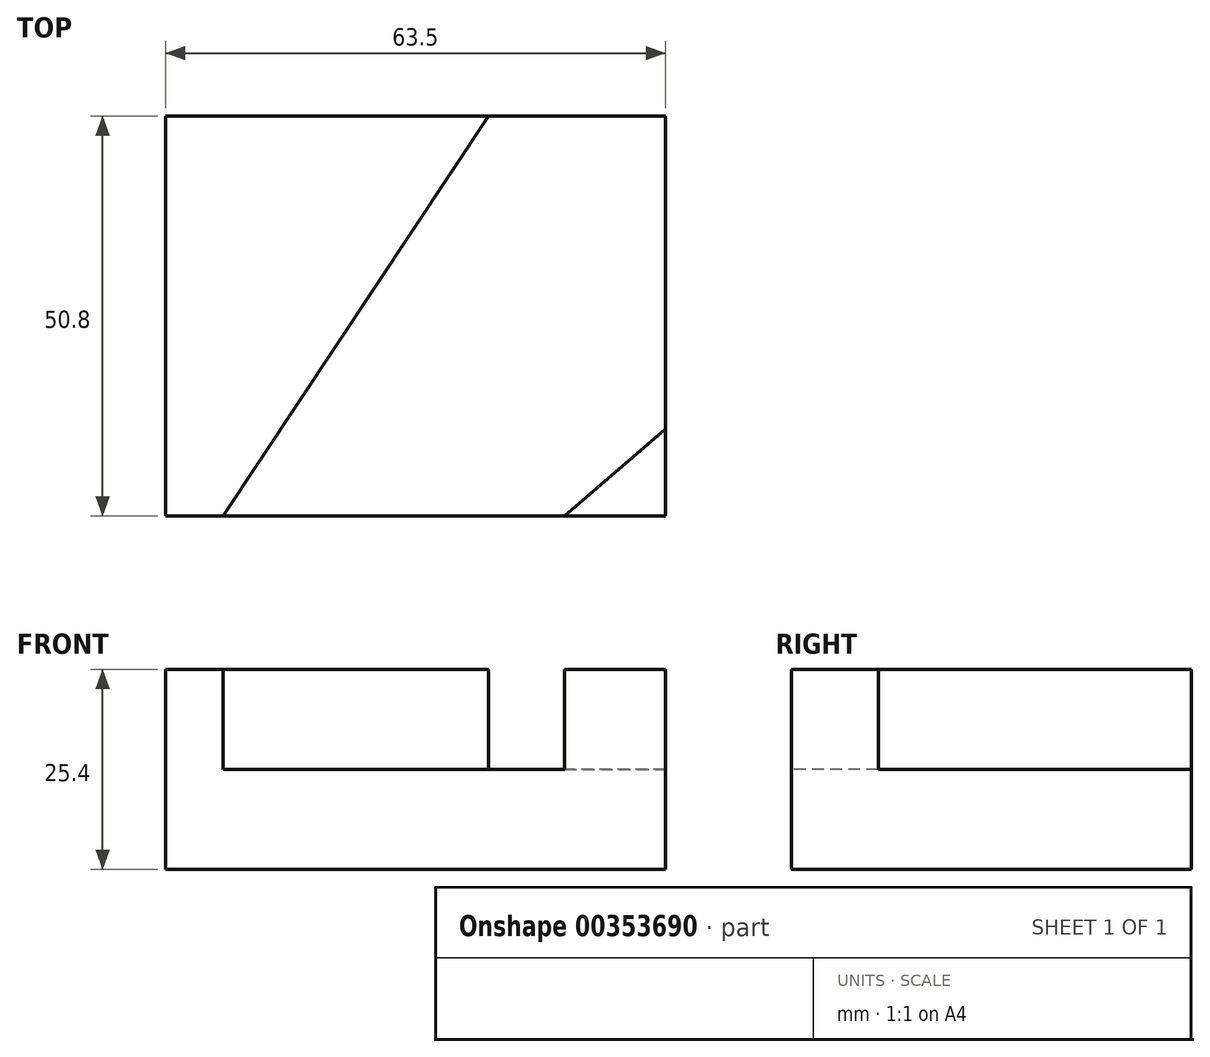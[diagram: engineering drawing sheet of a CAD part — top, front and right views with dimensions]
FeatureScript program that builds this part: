
annotation { "Feature Type Name" : "Feature", "Feature Type Description" : "" }
export const myFeature = defineFeature(function(context is Context, id is Id, definition is map)
    precondition{}
    {
        {
            var Q0;
            Q0=qCreatedBy(makeId("Top.planeOp"),FACE);
            var sketch = newSketch(context, id + "F0", { "sketchPlane" : qUnion([Q0])});
            skLineSegment(sketch, "E0", {"start": v(-35.36, 3.74) * mm, "end": v(-35.36, -47.06) * mm});
            skLineSegment(sketch, "E1", {"start": v(-35.36, -47.06) * mm, "end": v(28.14, -47.06) * mm});
            skLineSegment(sketch, "E2", {"start": v(28.14, -47.06) * mm, "end": v(28.14, 3.74) * mm});
            skLineSegment(sketch, "E3", {"start": v(28.14, 3.74) * mm, "end": v(-35.36, 3.74) * mm});
            skSolve(sketch);
        }
        {
            var Q0;
            Q0 = qSketchRegion(id + "F0", true);
            extrude(context, id + "F1", {"entities" : qUnion([Q0]), "depth" : 25.4 * mm});
        }
        {
            var Q0;
            Q0=makeQuery(id+"F1.opExtrude","CAP_FACE",FACE,{"disambiguationData":[OSD([sQuery(id+"F0.wireOp",EDGE,"E0"),sQuery(id+"F0.wireOp",EDGE,"E1"),sQuery(id+"F0.wireOp",EDGE,"E2"),sQuery(id+"F0.wireOp",EDGE,"E3")])],"isStart":false});
            var sketch = newSketch(context, id + "F2", { "sketchPlane" : qUnion([Q0])});
            skLineSegment(sketch, "E4", {"start": v(5.67, 3.74) * mm, "end": v(-28.09, -47.06) * mm});
            skLineSegment(sketch, "E5", {"start": v(-28.09, -47.06) * mm, "end": v(15.32, -47.06) * mm});
            skLineSegment(sketch, "E6", {"start": v(15.32, -47.06) * mm, "end": v(28.14, -36.03) * mm});
            skLineSegment(sketch, "E7", {"start": v(28.14, -36.03) * mm, "end": v(28.14, 3.74) * mm});
            skLineSegment(sketch, "E8", {"start": v(28.14, 3.74) * mm, "end": v(5.67, 3.74) * mm});
            skSolve(sketch);
        }
        {
            var Q0;
            Q0=makeQuery(id+"F2.imprint","IMPRINT",FACE,{"disambiguationData":[TD([[makeQuery(id+"F2.imprint","IMPRINT",EDGE,{"derivedFrom":sQuery(id+"F2.wireOp",EDGE,"E4")}),1.0]])]});
            extrude(context, id + "F3", {"entities" : qUnion([Q0]), "operationType" : NewBodyOperationType.REMOVE, "oppositeDirection" : true, "depth" : 12.7 * mm});
        }
    });
